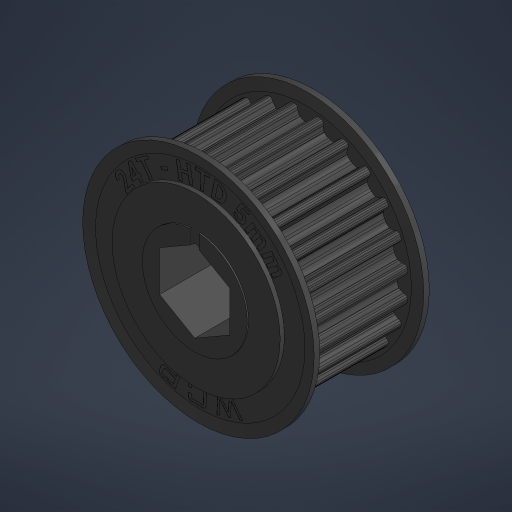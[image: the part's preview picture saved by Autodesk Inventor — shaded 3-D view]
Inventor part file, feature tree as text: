
AUTODESK INVENTOR PART (.ipt)
format: ipt  version: 2023.4 (Build 274418000, 418)  size: 899,584 bytes
history: native  units: mm (DEFAULTED — no unit token found)
features: mirror x2, delete_face x1, other x1
ambient origin geometry x8: Origin, YZ Plane, XZ Plane, XY Plane, X Axis, Y Axis, Z Axis, Center Point
bodies: Solid1 (feature_tree), Solid2 (feature_tree), Solid3 (feature_tree)
feature tree (4):
  delete_face  "Delete Face1"
  mirror  "Mirror2"
  mirror  "Mirror1"
  other  "Cut-Extrude5"
